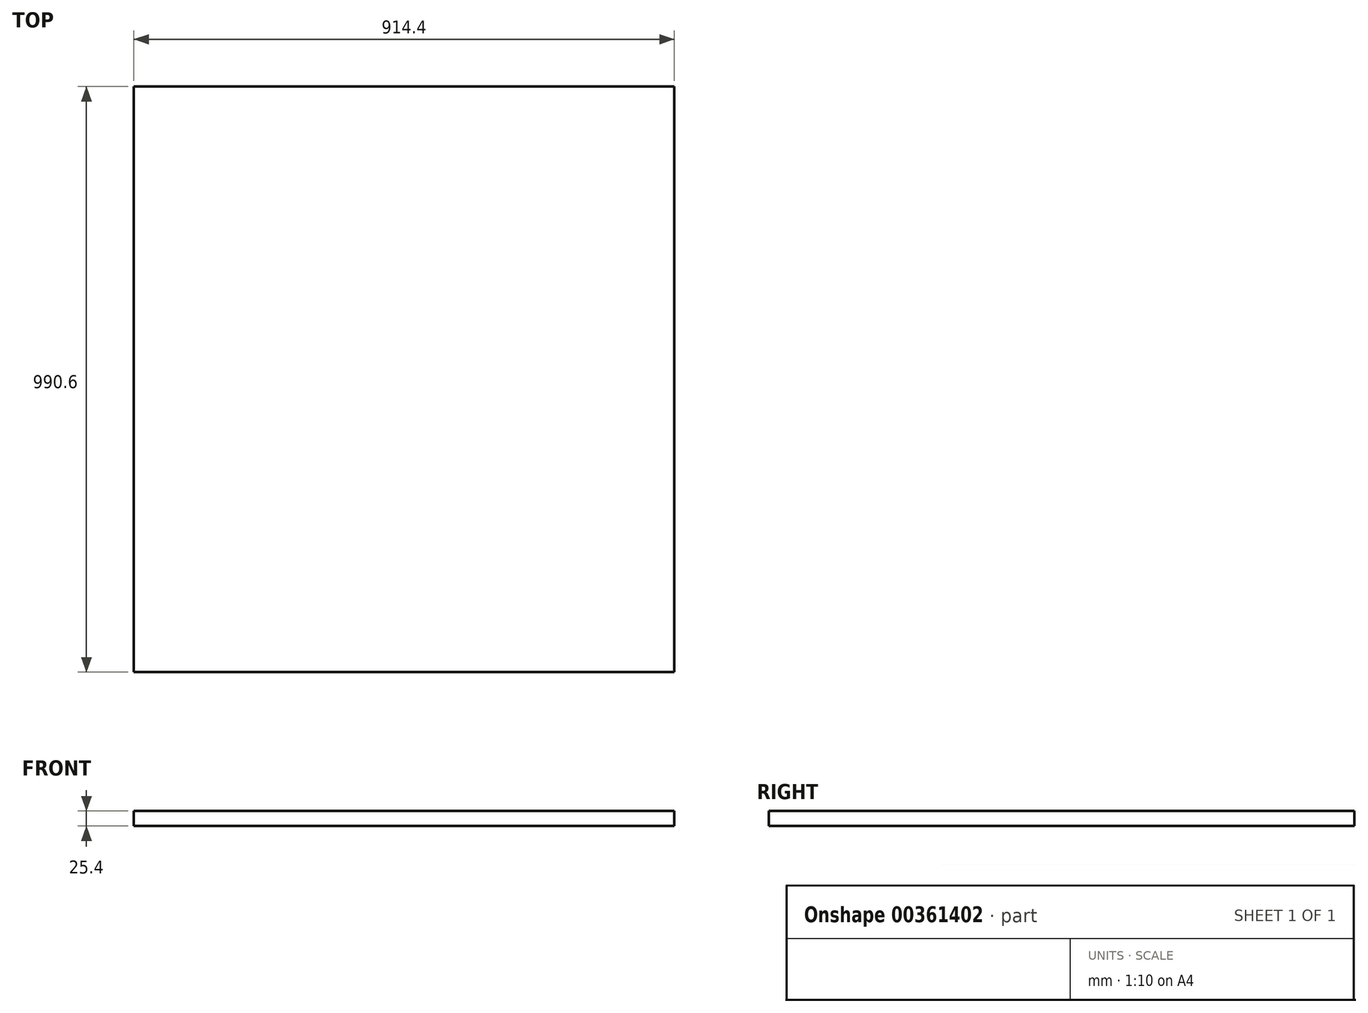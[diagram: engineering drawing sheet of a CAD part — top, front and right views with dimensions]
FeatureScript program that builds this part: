
annotation { "Feature Type Name" : "Feature", "Feature Type Description" : "" }
export const myFeature = defineFeature(function(context is Context, id is Id, definition is map)
    precondition{}
    {
        {
            var Q0;
            Q0=qCreatedBy(makeId("Top.planeOp"),FACE);
            var sketch = newSketch(context, id + "F0", { "sketchPlane" : qUnion([Q0])});
            skLineSegment(sketch, "E0.bottom", {"start": v(0, 0) * mm, "end": v(914.4, 0) * mm});
            skLineSegment(sketch, "E0.top", {"start": v(0, -990.6) * mm, "end": v(914.4, -990.6) * mm});
            skLineSegment(sketch, "E0.left", {"start": v(0, 0) * mm, "end": v(0, -990.6) * mm});
            skLineSegment(sketch, "E0.right", {"start": v(914.4, 0) * mm, "end": v(914.4, -990.6) * mm});
            skSolve(sketch);
        }
        {
            var Q0;
            Q0=makeQuery(id+"F0.imprint","IMPRINT",FACE,{"disambiguationData":[TD([[makeQuery(id+"F0.imprint","IMPRINT",EDGE,{"derivedFrom":sQuery(id+"F0.wireOp",EDGE,"E0.bottom")}),-1.0]])]});
            extrude(context, id + "F1", {"entities" : qUnion([Q0]), "depth" : 25.4 * mm});
        }
    });
